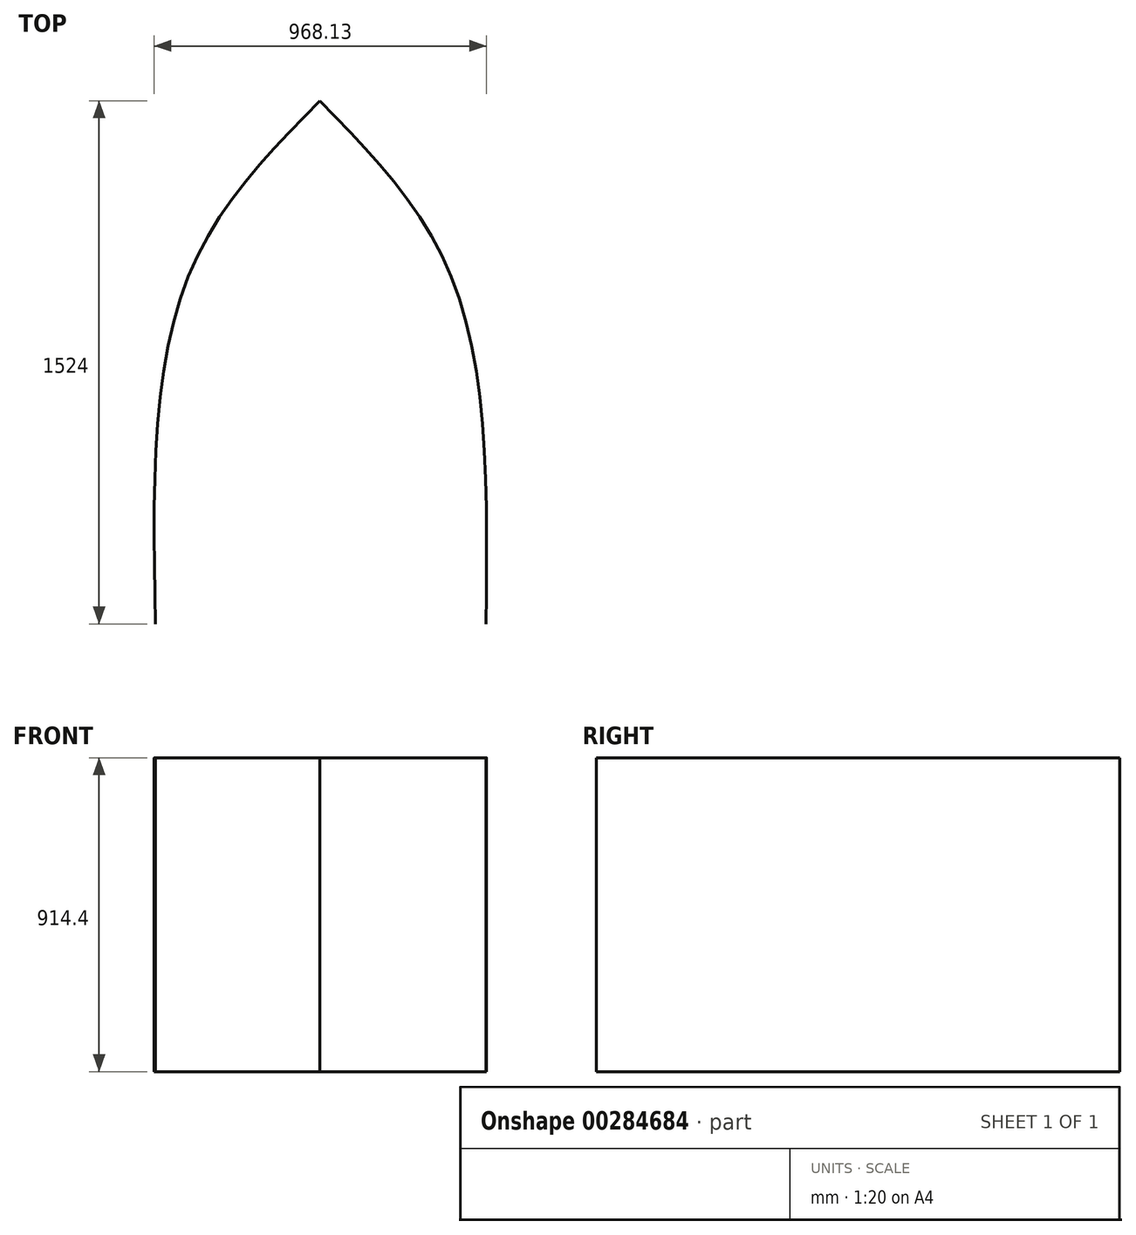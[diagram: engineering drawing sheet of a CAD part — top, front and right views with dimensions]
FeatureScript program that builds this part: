
annotation { "Feature Type Name" : "Feature", "Feature Type Description" : "" }
export const myFeature = defineFeature(function(context is Context, id is Id, definition is map)
    precondition{}
    {
        {
            var Q0;
            Q0=qCreatedBy(makeId("Top.planeOp"),FACE);
            var sketch = newSketch(context, id + "F0", { "sketchPlane" : qUnion([Q0])});
            skLineSegment(sketch, "E0", {"start": v(0, 0) * mm, "end": v(0, 914.4) * mm});
            skLineSegment(sketch, "E1", {"start": v(0, 914.4) * mm, "end": v(-391.16, 914.4) * mm});
            skLineSegment(sketch, "E2", {"start": v(0, 914.4) * mm, "end": v(391.16, 914.4) * mm});
            skLineSegment(sketch, "E3", {"start": v(-391.16, 914.4) * mm, "end": v(-391.16, 990.6) * mm});
            skLineSegment(sketch, "E4", {"start": v(-391.16, 990.6) * mm, "end": v(391.16, 990.6) * mm});
            skLineSegment(sketch, "E5", {"start": v(391.16, 990.6) * mm, "end": v(391.16, 914.4) * mm});
            skLineSegment(sketch, "E6", {"start": v(0, 914.4) * mm, "end": v(0, 1524) * mm});
            skFitSpline(sketch, "E7", {"points": [v(0, 1524) * mm, v(391.16, 990.6) * mm, v(483.99, 0) * mm], "startDerivative": vector(1028.63, -1050.44) * mm, "endDerivative": vector(-24.94, -1966.5) * mm});
            skFitSpline(sketch, "E8", {"points": [v(0, 1524) * mm, v(-391.16, 990.6) * mm, v(-478.87, 0) * mm], "startDerivative": vector(-1030.6, -1050.19) * mm, "endDerivative": vector(36.72, -1966.77) * mm});
            skLineSegment(sketch, "E9", {"start": v(483.99, 0) * mm, "end": v(-478.87, 0) * mm});
            skSolve(sketch);
        }
        {
            var Q0;
            Q0=sQuery(id+"F0.wireOp",EDGE,"E7");
            var Q1;
            Q1=sQuery(id+"F0.wireOp",EDGE,"E8");
            extrude(context, id + "F1", {"bodyType" : ToolBodyType.SURFACE, "surfaceEntities" : qUnion([Q0, Q1]), "oppositeDirection" : true, "depth" : 914.4 * mm});
        }
    });
